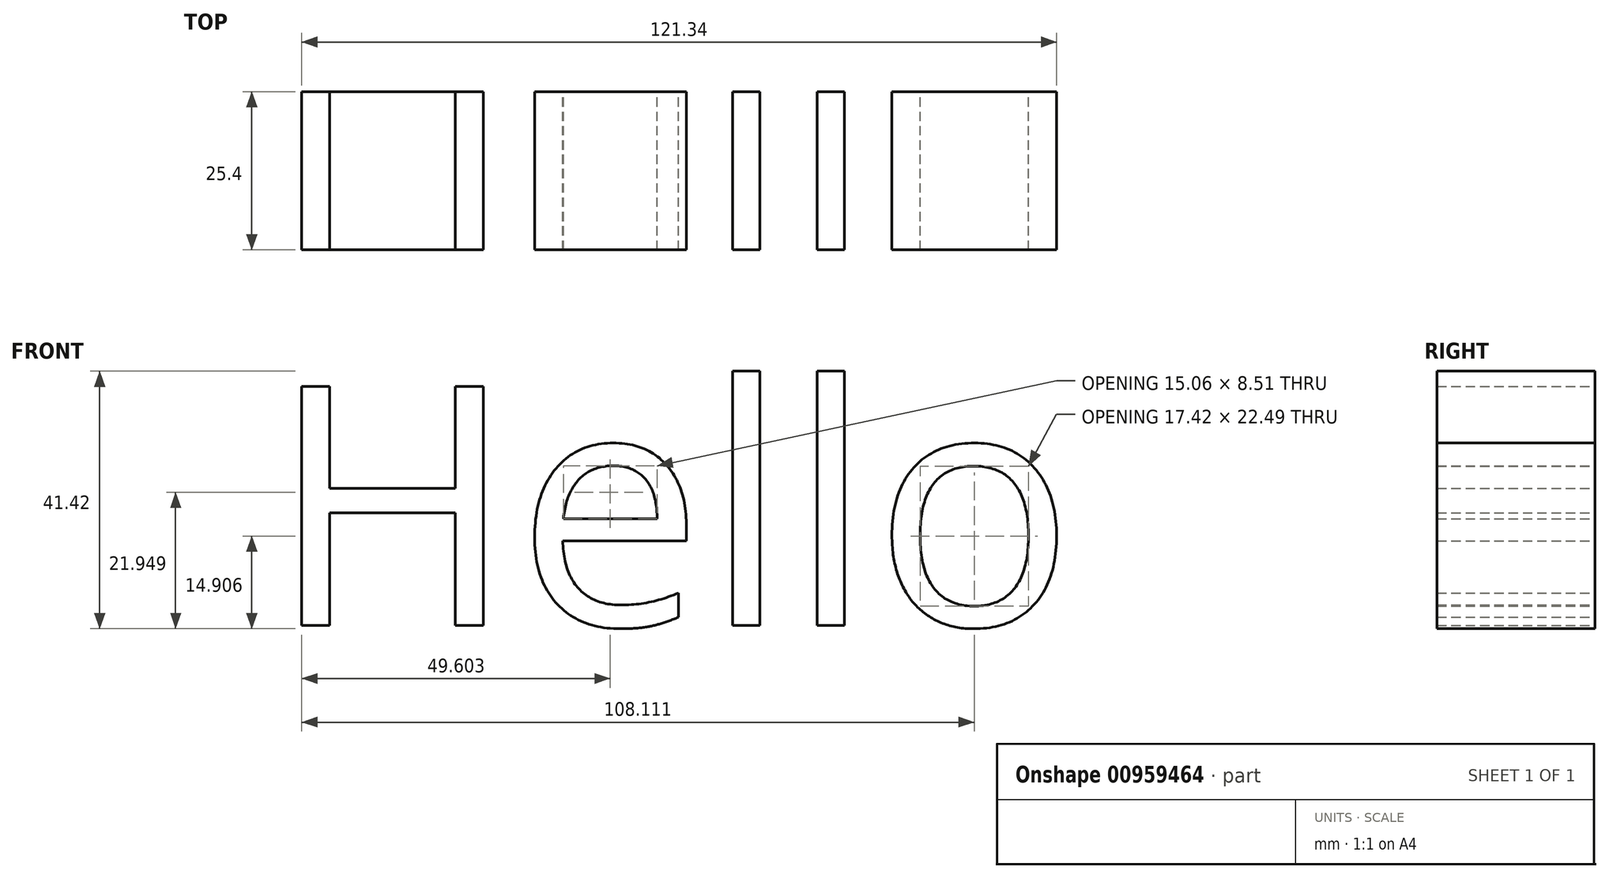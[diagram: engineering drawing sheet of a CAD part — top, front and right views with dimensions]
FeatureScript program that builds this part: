
annotation { "Feature Type Name" : "Feature", "Feature Type Description" : "" }
export const myFeature = defineFeature(function(context is Context, id is Id, definition is map)
    precondition{}
    {
        {
            var Q0;
            Q0=qCreatedBy(makeId("Front.planeOp"),FACE);
            var sketch = newSketch(context, id + "F0", { "sketchPlane" : qUnion([Q0])});
            skText(sketch, "E0", { "text": "Hello", "fontName": "OpenSans-Regular.ttf"});
            const initialGuessF0  = {"E0": [-0.1301, -0.03875, 1, 0, 0.03875]};
            skSetInitialGuess(sketch, initialGuessF0);
            skSolve(sketch);
        }
        {
            var Q0;
            Q0 = qSketchRegion(id + "F0", true);
            extrude(context, id + "F1", {"entities" : qUnion([Q0]), "depth" : 25.4 * mm, "offsetDistance" : 25.4 * mm});
        }
    });
